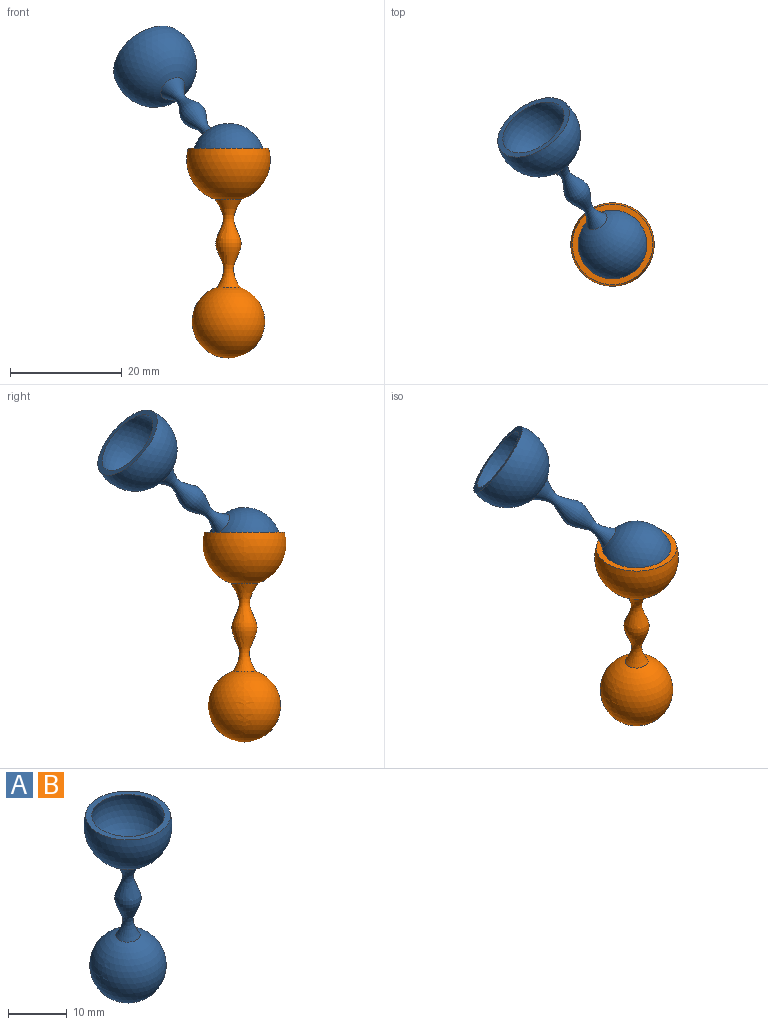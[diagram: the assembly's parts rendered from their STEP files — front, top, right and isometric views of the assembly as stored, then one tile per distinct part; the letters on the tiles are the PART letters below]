
ASSEMBLY  parts=2 mates=1
PART A: 5 faces, bbox 15x15x37.6 mm
  f0: sphere r=6.5mm, area 350.1mm2, adj f1
  f1: plane 14.42x14.42mm, normal (0,0,1), area 44mm2, adj f0,f2
  f2: sphere r=7.5mm, area 432.5mm2, adj f1,f3
  f3: revolved ~15.73x4.8mm, area 160mm2, adj f2,f4
  f4: sphere r=6.5mm, area 517.4mm2, adj f3
PART B: same geometry as A
PLACE A rot(axis=(0.17,-0.44,-0.88),156.6deg) t=(-7.87,-37.64,27.63)mm
PLACE B t=(-20.24,-19.36,-12.71)mm fixed
MATE ball A.f0 <-> B.f0  axis (-0.46,0.67,0.58) through (-20.24,-19.36,43.43)mm
